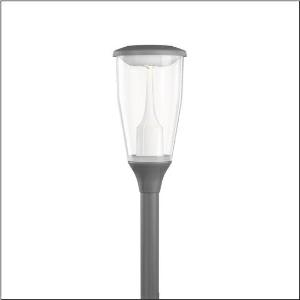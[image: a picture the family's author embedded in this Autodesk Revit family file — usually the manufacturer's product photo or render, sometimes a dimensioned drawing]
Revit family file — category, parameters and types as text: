
# Revit family: dl_11_iq___st1_2a_5xa5565af14h000022_cb01
name_source: partatom
category: Lighting Fixtures
units: mm (PartAtom-declared; Revit-internal decimal feet)

## family parameters
Cut with Voids When Loaded = No
Host = Face
Light Source = No
Part Type = Normal
Room Calculation Point = No
Round Connector Dimension = Use Diameter
Shared = No

## types (1)
- --- (1 x LED, 1560 lm, 12.9 W, 2200K)
    Apparent Load = 13 VA
    CIE Flux Codes = 24 63 94 96 100
    Color Rendering = 70
    Color Temperature = 2200K
    Default Elevation = 1800 mm
    Description = DL 11 iQ, mast luminaire, Module 540 iQ-SR, primary light control with 3 zone facetted reflector, of plastic, silver coated, highly specular, structured, primary optical cover: cover, of PMMA, transparent, light distribution: ST1.2a, light emission: direct distribution, primary light characteristic: asymmetric, installation type: post-top, LED, High Power LED, rated luminous flux: 1.560lm, luminous efficacy: 149lm/W, light colour: 722, colour temperature: 2200K, control: Street-Remote, Auto-Match, Temp-Guard, Lumen-Switch, Night-Set, Smart-Wire, Light-Fading, Desk-Remote (wireless, voltage-free reading and setting of iQ features in the workshop via application-optimized NFC function/RFID function), optimised constant luminous flux control (CLO 2.0), mains connection: 220..240V, AC, 50/60Hz, connection cable pre-assembled, cable length: 5,5m, start of lifetime: 13W, end of service life: 13W, reduction: 5W, luminaire housing, upper part, of diecast aluminium, coated, Siteco® metallic grey (DB 702S), spigot size: 60mm (post-top), post-top mast mounting element, of diecast aluminium, coated, Siteco® metallic grey (DB 702S), Module 540 iQ-SR, traffic white (RAL 9016), equipment: standard, protection rating (complete): IP66, insulation class (complete): insulation class II (safety insulation), certification: CE, ENEC, ENEC+, VDE, packaging unit: 1 piece

Light Distribution: ST1.2a
    Height = 665 mm
    Lamp = 1 x LED
    Lamp Light Flux = 1560 lm
    Lamp Power = 12.9 W
    Lamp count = 1
    Length = 334 mm
    Luminous efficacy = 121 lm/W
    Manufacturer = Siteco
    ModVariant = No
    Model = 5XA5565AF14H000022
    Number of Poles = 1
    OnlyDefault = Yes
    Power Factor = 1
    Product Name = DL 11 iQ | ST1.2a
    Product group = mast luminaire | pylon top
    ProductGroupID = 6100
    Protection Class = Protection class II
    Protection Degree = IP 66
    RLX_Detail_Level = 1
    RLX_Emergency_Light_Flux = 0 lm
    RLX_Emergency_Type = 0
    RLX_Emergency_Type_DB = No
    RlxData = <blob elided: 153533 chars, md5=8e390ddf>
    Socket = socket
    Standby Power = 0 W
    System Light Flux = 1560 lm
    System Power = 13 W
    Type Comments = factory setting: luminous flux: 100 % | dim-lin: 254 | 516 mA
    Type Image = l_1258354.jpg
    URL = http://relux.com
    VarID = @adj_025935
    Voltage = 0 V
    Weight = 0.00 kg
    Width = 0 mm  [stored 0 ft]

note: [stored X ft] marks values corroborated as IEEE doubles in the binary element streams (Revit-internal decimal feet)

## geometry (parser evidence)
native form markers: Blend x4, Sweep x9
no freeform markers — native parametric forms only
